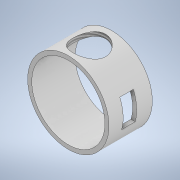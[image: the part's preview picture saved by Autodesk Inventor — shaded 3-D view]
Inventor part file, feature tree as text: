
AUTODESK INVENTOR PART (.ipt)
format: ipt  version: 2021 (Build 250183000, 183)  size: 138,240 bytes
history: native  units: mm
features: extrude x3, sketch x3, other x1
ambient origin geometry x8: Origin, YZ Plane, XZ Plane, XY Plane, X Axis, Y Axis, Z Axis, Center Point
bodies: Solide1 (feature_tree)
feature tree (7):
  extrude  "Extrusion1"  Depth=60.0mm
  extrude  "Extrusion2"  Depth=54.0mm
  other  "Filetage1"
  extrude  "Extrusion3"  Depth=32.0mm TaperAngle=0.0deg
  sketch  "Esquisse1"
  sketch  "Esquisse2"
  sketch  "Esquisse3"
